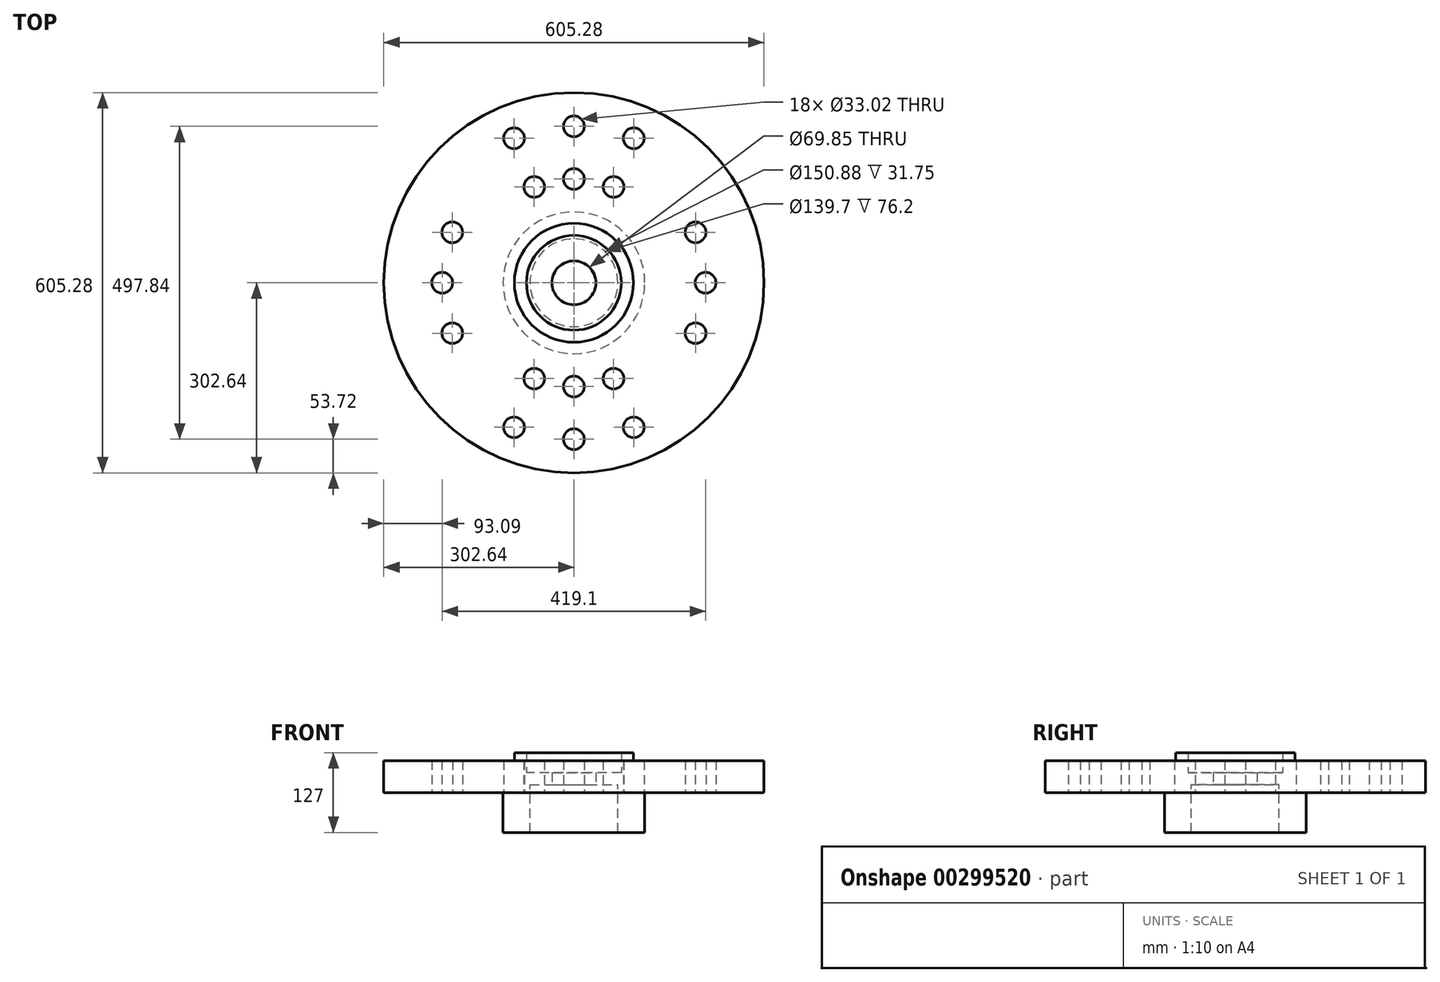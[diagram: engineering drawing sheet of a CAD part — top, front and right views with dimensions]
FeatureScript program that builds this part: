
annotation { "Feature Type Name" : "Feature", "Feature Type Description" : "" }
export const myFeature = defineFeature(function(context is Context, id is Id, definition is map)
    precondition{}
    {
        {
            var Q0;
            Q0=qCreatedBy(makeId("Top.planeOp"),FACE);
            var sketch = newSketch(context, id + "F0", { "sketchPlane" : qUnion([Q0])});
            skCircle(sketch, "E0", {"center": v(0, 0) * mm, "radius": 302.64 * mm});
            skLineSegment(sketch, "E1", {"start": v(0, 0) * mm, "end": v(0, 389.6) * mm});
            skLineSegment(sketch, "E2.MirrorCS", {"start": v(0, 0) * mm, "end": v(432.17, 85.96) * mm});
            skLineSegment(sketch, "E3", {"start": v(0, 0) * mm, "end": v(77.77, 390.97) * mm});
            skCircle(sketch, "E4", {"center": v(0, 165.1) * mm, "radius": 16.51 * mm});
            skCircle(sketch, "E5", {"center": v(0, 248.92) * mm, "radius": 16.51 * mm});
            skCircle(sketch, "E6.MirrorC", {"center": v(95.26, 229.97) * mm, "radius": 16.51 * mm});
            skCircle(sketch, "E7.MirrorC", {"center": v(63.18, 152.53) * mm, "radius": 16.51 * mm});
            skLineSegment(sketch, "E8", {"start": v(0, 0) * mm, "end": v(479.48, 0) * mm});
            skCircle(sketch, "E9", {"center": v(209.55, 0) * mm, "radius": 16.51 * mm});
            skCircle(sketch, "E10.MirrorC", {"center": v(193.6, 80.2) * mm, "radius": 16.51 * mm});
            skCircle(sketch, "E11.MirrorC", {"center": v(-95.26, 229.97) * mm, "radius": 16.51 * mm});
            skCircle(sketch, "E12.MirrorC", {"center": v(-63.18, 152.53) * mm, "radius": 16.51 * mm});
            skCircle(sketch, "E13.MirrorC", {"center": v(-193.6, 80.2) * mm, "radius": 16.51 * mm});
            skCircle(sketch, "E14.MirrorC", {"center": v(-209.55, 0) * mm, "radius": 16.51 * mm});
            skCircle(sketch, "E15.MirrorC", {"center": v(-193.6, -80.2) * mm, "radius": 16.51 * mm});
            skCircle(sketch, "E16.MirrorC", {"center": v(-63.18, -152.53) * mm, "radius": 16.51 * mm});
            skCircle(sketch, "E17.MirrorC", {"center": v(-95.26, -229.97) * mm, "radius": 16.51 * mm});
            skCircle(sketch, "E18.MirrorC", {"center": v(0, -248.92) * mm, "radius": 16.51 * mm});
            skCircle(sketch, "E19.MirrorC", {"center": v(0, -165.1) * mm, "radius": 16.51 * mm});
            skCircle(sketch, "E20.MirrorC", {"center": v(95.26, -229.97) * mm, "radius": 16.51 * mm});
            skCircle(sketch, "E21.MirrorC", {"center": v(63.18, -152.53) * mm, "radius": 16.51 * mm});
            skCircle(sketch, "E22.MirrorC", {"center": v(193.6, -80.2) * mm, "radius": 16.51 * mm});
            skCircle(sketch, "E23", {"center": v(0, 0) * mm, "radius": 34.93 * mm});
            skSolve(sketch);
        }
        {
            var Q0;
            Q0 = qSketchRegion(id + "F0", true);
            extrude(context, id + "F1", {"entities" : qUnion([Q0]), "depth" : 50.8 * mm});
        }
        {
            var Q0;
            Q0=makeQuery(id+"F1.opExtrude","CAP_FACE",FACE,{"disambiguationData":[OSD([sQuery(id+"F0.wireOp",EDGE,"E0"),sQuery(id+"F0.wireOp",EDGE,"E4"),sQuery(id+"F0.wireOp",EDGE,"E5"),sQuery(id+"F0.wireOp",EDGE,"E6.MirrorC"),sQuery(id+"F0.wireOp",EDGE,"E7.MirrorC"),sQuery(id+"F0.wireOp",EDGE,"E10.MirrorC"),sQuery(id+"F0.wireOp",EDGE,"E11.MirrorC"),sQuery(id+"F0.wireOp",EDGE,"E12.MirrorC"),sQuery(id+"F0.wireOp",EDGE,"E13.MirrorC"),sQuery(id+"F0.wireOp",EDGE,"E14.MirrorC"),sQuery(id+"F0.wireOp",EDGE,"E15.MirrorC"),sQuery(id+"F0.wireOp",EDGE,"E16.MirrorC"),sQuery(id+"F0.wireOp",EDGE,"E17.MirrorC"),sQuery(id+"F0.wireOp",EDGE,"E18.MirrorC"),sQuery(id+"F0.wireOp",EDGE,"E19.MirrorC"),sQuery(id+"F0.wireOp",EDGE,"E20.MirrorC"),sQuery(id+"F0.wireOp",EDGE,"E21.MirrorC"),sQuery(id+"F0.wireOp",EDGE,"E22.MirrorC"),sQuery(id+"F0.wireOp",EDGE,"E9"),sQuery(id+"F0.wireOp",EDGE,"E23")])],"isStart":false});
            var sketch = newSketch(context, id + "F2", { "sketchPlane" : qUnion([Q0])});
            skCircle(sketch, "E24", {"center": v(0, 0) * mm, "radius": 94.74 * mm});
            skCircle(sketch, "E25", {"center": v(0, 0) * mm, "radius": 75.44 * mm});
            skSolve(sketch);
        }
        {
            var Q0;
            Q0 = qSketchRegion(id + "F2", true);
            extrude(context, id + "F3", {"entities" : qUnion([Q0]), "operationType" : NewBodyOperationType.ADD, "depth" : 12.7 * mm});
        }
        {
            var Q0;
            Q0=makeQuery(id+"F3.opExtrude","CAP_FACE",FACE,{"disambiguationData":[OSD([sQuery(id+"F2.wireOp",EDGE,"E24"),sQuery(id+"F2.wireOp",EDGE,"E25")])],"isStart":false});
            var sketch = newSketch(context, id + "F4", { "sketchPlane" : qUnion([Q0])});
            skCircle(sketch, "E26", {"center": v(0, 0) * mm, "radius": 75.44 * mm});
            skSolve(sketch);
        }
        {
            var Q0;
            Q0 = qSketchRegion(id + "F4", true);
            extrude(context, id + "F5", {"entities" : qUnion([Q0]), "operationType" : NewBodyOperationType.REMOVE, "endBound" : BoundingType.SYMMETRIC, "depth" : 63.5 * mm});
        }
        {
            var Q0;
            Q0=makeQuery(id+"F1.opExtrude","CAP_FACE",FACE,{"disambiguationData":[OSD([sQuery(id+"F0.wireOp",EDGE,"E0"),sQuery(id+"F0.wireOp",EDGE,"E4"),sQuery(id+"F0.wireOp",EDGE,"E5"),sQuery(id+"F0.wireOp",EDGE,"E6.MirrorC"),sQuery(id+"F0.wireOp",EDGE,"E7.MirrorC"),sQuery(id+"F0.wireOp",EDGE,"E10.MirrorC"),sQuery(id+"F0.wireOp",EDGE,"E11.MirrorC"),sQuery(id+"F0.wireOp",EDGE,"E12.MirrorC"),sQuery(id+"F0.wireOp",EDGE,"E13.MirrorC"),sQuery(id+"F0.wireOp",EDGE,"E14.MirrorC"),sQuery(id+"F0.wireOp",EDGE,"E15.MirrorC"),sQuery(id+"F0.wireOp",EDGE,"E16.MirrorC"),sQuery(id+"F0.wireOp",EDGE,"E17.MirrorC"),sQuery(id+"F0.wireOp",EDGE,"E18.MirrorC"),sQuery(id+"F0.wireOp",EDGE,"E19.MirrorC"),sQuery(id+"F0.wireOp",EDGE,"E20.MirrorC"),sQuery(id+"F0.wireOp",EDGE,"E21.MirrorC"),sQuery(id+"F0.wireOp",EDGE,"E22.MirrorC"),sQuery(id+"F0.wireOp",EDGE,"E9"),sQuery(id+"F0.wireOp",EDGE,"E23")])],"isStart":true});
            var sketch = newSketch(context, id + "F6", { "sketchPlane" : qUnion([Q0])});
            skCircle(sketch, "E27", {"center": v(0, 0) * mm, "radius": 69.85 * mm});
            skCircle(sketch, "E28", {"center": v(0, 0) * mm, "radius": 112.78 * mm});
            skSolve(sketch);
        }
        {
            var Q0;
            Q0 = qSketchRegion(id + "F6", true);
            extrude(context, id + "F7", {"entities" : qUnion([Q0]), "operationType" : NewBodyOperationType.ADD, "depth" : 63.5 * mm});
        }
        {
            var Q0;
            Q0=makeQuery(id+"F7.opExtrude","CAP_FACE",FACE,{"disambiguationData":[OSD([sQuery(id+"F6.wireOp",EDGE,"E27"),sQuery(id+"F6.wireOp",EDGE,"E28")])],"isStart":false});
            var sketch = newSketch(context, id + "F8", { "sketchPlane" : qUnion([Q0])});
            skCircle(sketch, "E29", {"center": v(0, 0) * mm, "radius": 69.85 * mm});
            skSolve(sketch);
        }
        {
            var Q0;
            Q0 = qSketchRegion(id + "F8", true);
            extrude(context, id + "F9", {"entities" : qUnion([Q0]), "operationType" : NewBodyOperationType.REMOVE, "oppositeDirection" : true, "depth" : 76.2 * mm});
        }
    });
